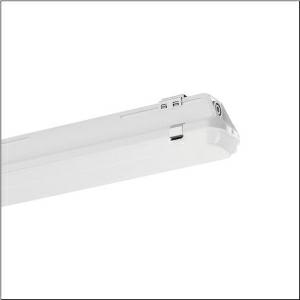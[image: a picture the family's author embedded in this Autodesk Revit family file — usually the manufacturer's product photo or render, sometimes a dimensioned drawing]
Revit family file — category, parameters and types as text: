
# Revit family: monsun_11_parking_51fg20dp440l007
name_source: partatom
category: Lighting Fixtures
units: mm (PartAtom-declared; Revit-internal decimal feet)

## family parameters
Cut with Voids When Loaded = No
Host = Face
Light Source = No
Part Type = Normal
Room Calculation Point = No
Round Connector Dimension = Use Diameter
Shared = No

## types (1)
- --- (1 x LED, 4840 lm, 28.1 W, 4000K)
    Apparent Load = 28 VA
    CIE Flux Codes = 45 75 93 94 100
    Color Rendering = 80
    Color Temperature = 4000K
    Default Elevation = 1800 mm
    Description = Monsun 11 parking, damp-proof luminaire, chain hanger, primary optical cover: enclosure, of PC, light emission: direct distribution, primary light characteristic: symmetric, installation type: vertical mounting, horizontal mounting, surface-mounted, suspended mounting, LED, rated luminous flux: 4.840lm, luminous efficacy: 172lm/W, light colour: 840, colour temperature: 4000K, control gear: DALI 2, with terminal, 5-pole, max. 2.5mm², through-wiring: 7x 2.5mm², mains connection: 220..240V, AC, 50/60Hz, rated input power: 28W, housing, of glass-fibre reinforced polyester, uncoated, bright grey, incl. chain hanger, length: 1.590mm, width: 90mm, height: 88mm, clip for enclosure, of stainless steel (V2A), ceiling mounting element, of stainless steel (V2A), chain hanger, of stainless steel (V2A), protection rating (complete): IP66, insulation class (complete): insulation class I (protective earthing), certification: CE, ENEC, VDE, UKCA, protection symbol: D, impact resistance: IK08, permissible operating ambient temperature: -25..+35°C, standard: EN 50419, EN 60598-2-1, corresponds to IFS (International Featured Standards) requirements for safety and quality in the food industry, for indoor or canopied outdoor use, no direct snow, no direct sun, no direct rain, LABS conformity tested according to VDMA 24364:2018-05, contact your sales advisor before using the luminaires in applications with unclear chemical exposure, large temperature fluctuations or condensation-forming humidity, packaging unit: 1 piece
    Height = 89 mm
    Lamp = 1 x LED
    Lamp Light Flux = 4840 lm
    Lamp Power = 28.1 W
    Lamp count = 1
    Length = 1590 mm
    Luminous efficacy = 172 lm/W
    Manufacturer = Siteco
    ModVariant = No
    Model = 51FG20DP440L007
    Mounting Place = Ceiling
    Mounting Type = Surface mounted
    Number of Poles = 1
    OnlyDefault = Yes
    Power Factor = 1
    Product Name = Monsun 11 parking
    Product group = damp-proof luminaire
    ProductGroupID = 300
    Protection Class = Protection class I
    Protection Degree = IP 66
    RLX_Detail_Level = 1
    RLX_Emergency_Light_Flux = 0 lm
    RLX_Emergency_Type = 0
    RLX_Emergency_Type_DB = No
    RlxData = <blob elided: 92349 chars, md5=3c02b802>
    Socket = socket
    Standby Power = 0 W
    System Light Flux = 4840 lm
    System Power = 28 W
    Type Comments = factory setting: luminous flux: 100 % | dim-lin: 254 | 193 mA
    Type Image = l_1349237.jpg
    URL = http://relux.com
    VarID = @adj_033513
    Voltage = 0 V
    Weight = 0.00 kg
    Width = 90 mm

## geometry (parser evidence)
native form markers: Blend x4, Sweep x14
no freeform markers — native parametric forms only
